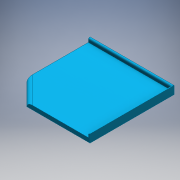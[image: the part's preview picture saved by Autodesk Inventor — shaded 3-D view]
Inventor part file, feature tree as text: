
AUTODESK INVENTOR PART (.ipt)
format: ipt  version: 2016 (Build 200138000, 138)  size: 140,288 bytes
history: native  units: mm
features: extrude x3, sketch x3, fillet x1
ambient origin geometry x8: Origin, YZ Plane, XZ Plane, XY Plane, X Axis, Y Axis, Z Axis, Center Point
bodies: Solid1 (feature_tree)
feature tree (7):
  extrude  "Extrusion1"  Depth=50.0mm
  fillet  "Fillet1"  Radius=20.0mm
  extrude  "Extrusion2"  Depth=20.0mm
  extrude  "Extrusion3"  Depth=20.0mm
  sketch  "Sketch1"  dims[d3=50.0mm d4=0.0mm d5=50.0mm d9=20.0mm]
  sketch  "Sketch3"  dims[d10=100.0mm d11=20.0mm]
  sketch  "Sketch4"  dims[d12=0.0mm d13=0.0mm d14=20.0mm d15=20.0mm d16=242.5mm d17=0.0mm d22=790.0mm d23=1050.0mm]
